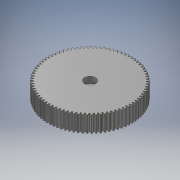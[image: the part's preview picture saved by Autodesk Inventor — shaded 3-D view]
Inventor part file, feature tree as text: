
AUTODESK INVENTOR PART (.ipt)
format: ipt  version: 2017 (Build 210142000, 142)  size: 521,728 bytes
history: native  units: mm (DEFAULTED — no unit token found)
features: sketch x5, extrude x4, plane x3, other x3, pattern_circular x1
ambient origin geometry x8: Origin, YZ Plane, XZ Plane, XY Plane, X Axis, Y Axis, Z Axis, Center Point
bodies: Solid1 (feature_tree)
feature tree (16):
  extrude  "Extrusion1"  Depth=20.0mm TaperAngle=0.0deg
  plane  "Work Plane2"
  plane  "Work Plane8"
  plane  "Work Plane9"
  other  "Spur Gear"
  extrude  "Extrusion2"  Depth=10.0mm TaperAngle=0.0deg
  extrude  "Extrusion3"  Depth=0.387851mm TaperAngle=0.0deg
  extrude  "Extrusion4"  TaperAngle=0.0deg  [1 undecoded]
  pattern_circular  "Circular Pattern1"  [2 undecoded]
  sketch  "Sketch1"  dims[d0=103.5mm d1=20.0mm d2=0.0mm]
  sketch  "Sketch2"  dims[d3=101.049505mm d4=10.0mm d5=0.0mm]
  other  "Srf1"
  sketch  "Sketch3"  dims[d16=63.0mm d17=0.0mm d34=0.387851mm]
  sketch  "Sketch4"  dims[d39=0.0mm d41=0.0mm]
  sketch  "Sketch5"  dims[d43=63.0mm d46=63.0mm d47=0.0mm d48=0.0mm d49=13.5mm d50=10.0mm d51=0.0mm d52=35.0mm d53=15.0mm d54=0.0mm d55=6.0mm d56=60.0deg d57=5.0mm d58=0.0mm d59=40.0mm d60=360.0deg]
  other  "Pitch Diameter"
note: 3 required parameter values undecoded (feature->parameter linkage not recoverable at this tier; creation-order binding heuristic only, values carry confidence <= 0.55)
